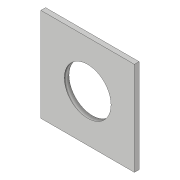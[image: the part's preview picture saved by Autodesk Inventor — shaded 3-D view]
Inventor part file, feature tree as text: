
AUTODESK INVENTOR PART (.ipt)
format: ipt  version: 2019 (Build 230136000, 136)  size: 87,040 bytes
history: native  units: in
note: dims shown in document units (in); Inventor stores cm internally (conversion verified against a paired STEP export)
features: extrude x2, sketch x2, thread x1
ambient origin geometry x8: Origin, YZ Plane, XZ Plane, XY Plane, X Axis, Y Axis, Z Axis, Center Point
bodies: Solid1 (feature_tree)
feature tree (5):
  extrude  "Extrusion1"  Depth=0.7874in
  extrude  "Extrusion2"  Depth=0.3937in
  thread  "Thread1"  [1 undecoded]
  sketch  "Sketch1"  dims[d0=0.7874in d1=0.7874in]
  sketch  "Sketch2"  dims[d2=0.0394in d3=0.0in d4=0.3937in d5=0.3937in d6=0.3937in d7=0.0394in d8=0.0in d9=0.3937in d10=0.0in]
note: 1 required parameter value undecoded (feature->parameter linkage not recoverable at this tier; creation-order binding heuristic only, values carry confidence <= 0.55)
